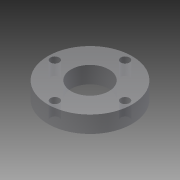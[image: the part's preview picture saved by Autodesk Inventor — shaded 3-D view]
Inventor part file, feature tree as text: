
AUTODESK INVENTOR PART (.ipt)
format: ipt  version: 2013 (Build 170138000, 138)  size: 91,648 bytes
history: native  units: in
note: dims shown in document units (in); Inventor stores cm internally (conversion verified against a paired STEP export)
features: extrude x1, sketch x1
ambient origin geometry x8: Origin, YZ Plane, XZ Plane, XY Plane, X Axis, Y Axis, Z Axis, Center Point
bodies: Solid1 (feature_tree)
feature tree (2):
  extrude  "Extrusion1"  Depth=2.09in
  sketch  "Sketch1"  dims[d0=1.125in d1=2.09in d2=2.5in d3=0.26in d4=0.26in d5=0.26in d6=0.26in d7=0.5in d8=0.0in]
